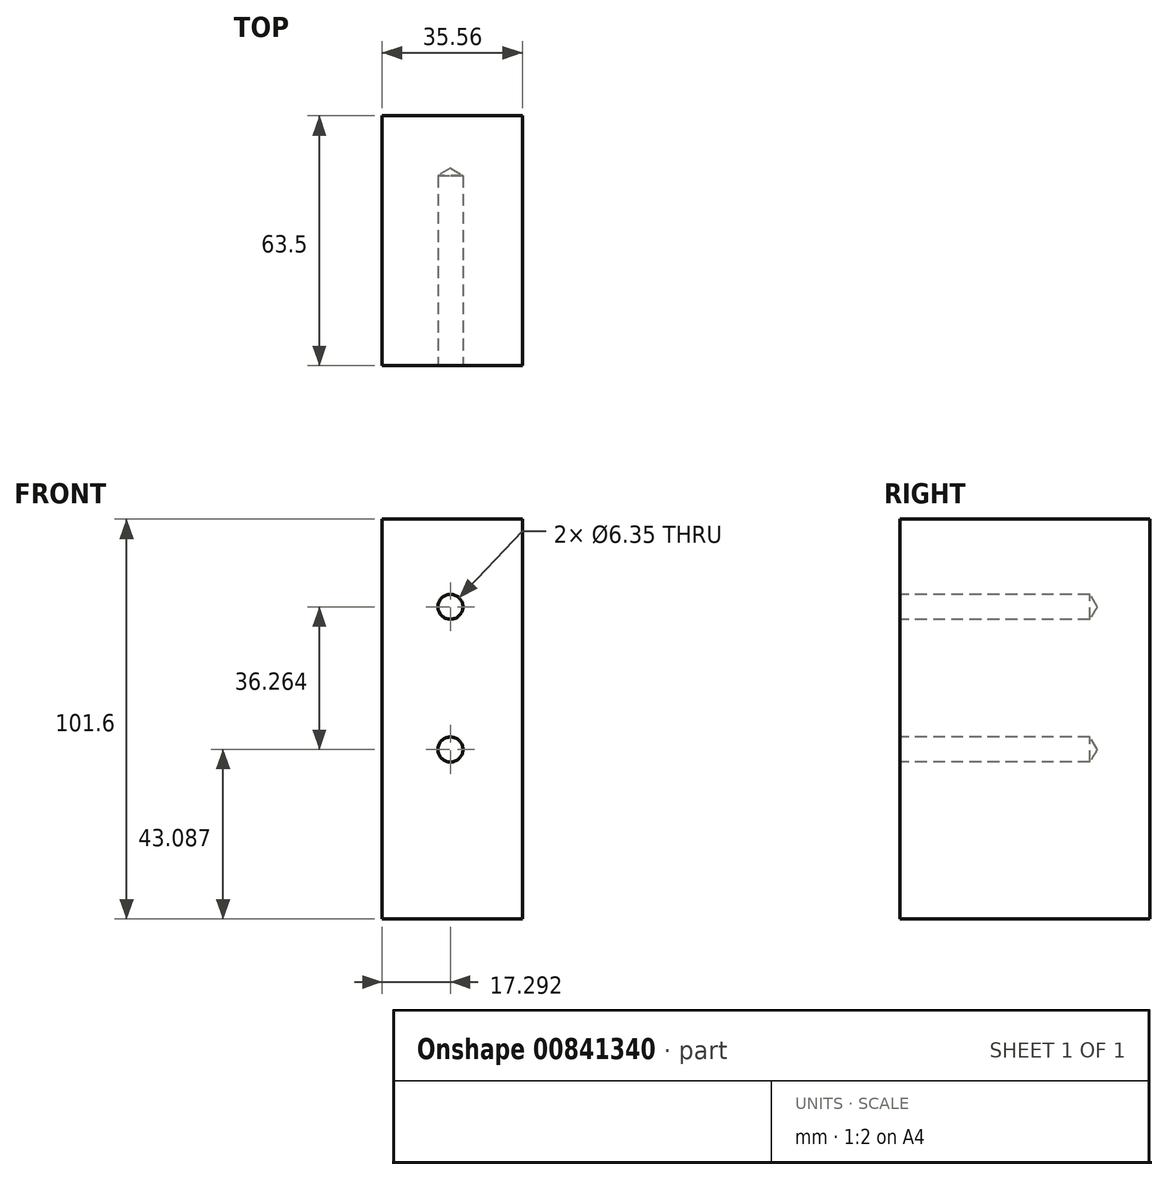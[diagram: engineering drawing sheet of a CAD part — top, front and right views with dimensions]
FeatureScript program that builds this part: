
annotation { "Feature Type Name" : "Feature", "Feature Type Description" : "" }
export const myFeature = defineFeature(function(context is Context, id is Id, definition is map)
    precondition{}
    {
        {
            var Q0;
            Q0=qCreatedBy(makeId("Front.planeOp"),FACE);
            var sketch = newSketch(context, id + "F0", { "sketchPlane" : qUnion([Q0])});
            skLineSegment(sketch, "E0.bottom", {"start": v(0, 0) * mm, "end": v(35.56, 0) * mm});
            skLineSegment(sketch, "E0.top", {"start": v(0, 101.6) * mm, "end": v(35.56, 101.6) * mm});
            skLineSegment(sketch, "E0.left", {"start": v(0, 0) * mm, "end": v(0, 101.6) * mm});
            skLineSegment(sketch, "E0.right", {"start": v(35.56, 0) * mm, "end": v(35.56, 101.6) * mm});
            skSolve(sketch);
        }
        {
            var Q0;
            Q0 = qSketchRegion(id + "F0", true);
            extrude(context, id + "F1", {"entities" : qUnion([Q0]), "depth" : 63.5 * mm, "offsetDistance" : 25.4 * mm});
        }
        {
            var Q0;
            Q0=makeQuery(id+"F1.opExtrude","CAP_FACE",FACE,{"disambiguationData":[OSD([sQuery(id+"F0.wireOp",EDGE,"E0.bottom"),sQuery(id+"F0.wireOp",EDGE,"E0.top"),sQuery(id+"F0.wireOp",EDGE,"E0.left"),sQuery(id+"F0.wireOp",EDGE,"E0.right")])],"isStart":false});
            var sketch = newSketch(context, id + "F2", { "sketchPlane" : qUnion([Q0])});
            skPoint(sketch, "E1", {"position": v(17.3, 43.09) * mm});
            skPoint(sketch, "E2", {"position": v(17.3, 79.35) * mm});
            skSolve(sketch);
        }
        {
            var Q0;
            Q0=sQuery(id+"F2.wireOp",VERTEX,"E1");
            var Q1;
            Q1=sQuery(id+"F2.wireOp",VERTEX,"E2");
            var Q2;
            Q2=makeQuery(id+"F1.opExtrude","SWEPT_BODY",BODY,{"disambiguationData":[OSD([sQuery(id+"F0.wireOp",EDGE,"E0.bottom"),sQuery(id+"F0.wireOp",EDGE,"E0.top"),sQuery(id+"F0.wireOp",EDGE,"E0.left"),sQuery(id+"F0.wireOp",EDGE,"E0.right")])]});
            hole(context, id + "F3", {"style" : HoleStyle.SIMPLE, "endStyle" : HoleEndStyle.BLIND, "holeDiameter" : 6.35 * mm, "majorDiameter" : 6.35 * mm, "holeDepth" : 48.26 * mm, "isTappedThrough" : true, "tappedDepth" : 12.7 * mm, "tapClearance" : 3, "locations" : qUnion([Q0, Q1]), "scope" : qUnion([Q2])});
        }
    });
